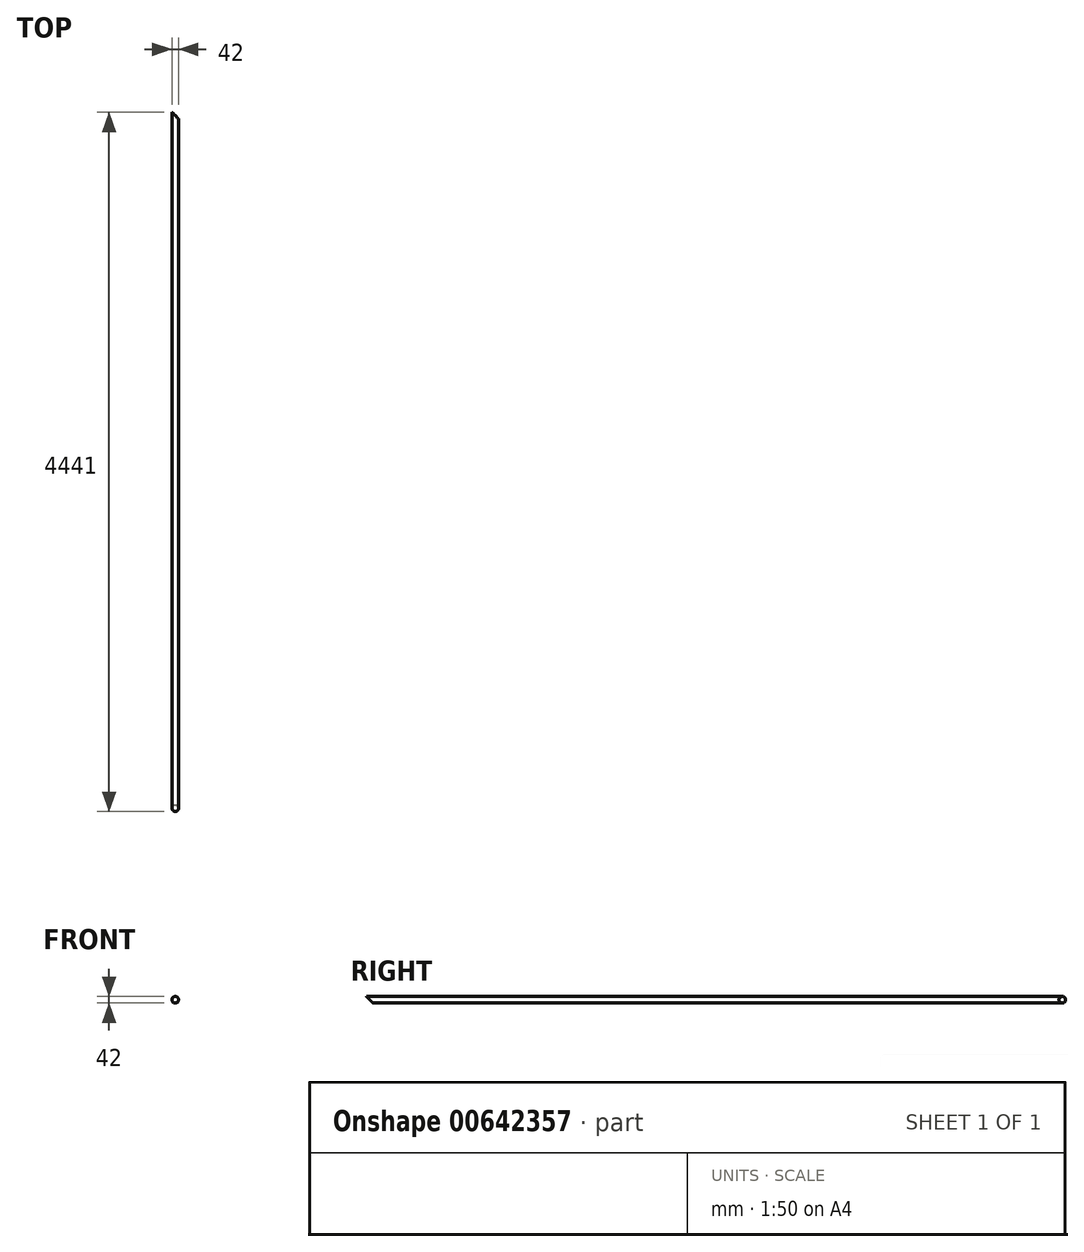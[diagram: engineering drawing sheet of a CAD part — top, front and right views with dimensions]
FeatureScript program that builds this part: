
annotation { "Feature Type Name" : "Feature", "Feature Type Description" : "" }
export const myFeature = defineFeature(function(context is Context, id is Id, definition is map)
    precondition{}
    {
        {
            var Q0;
            Q0=qCreatedBy(makeId("Front.planeOp"),FACE);
            var sketch = newSketch(context, id + "F0", { "sketchPlane" : qUnion([Q0])});
            skLineSegment(sketch, "E0.bottom", {"start": v(21, 21) * mm, "end": v(-21, 21) * mm});
            skLineSegment(sketch, "E0.top", {"start": v(21, -21) * mm, "end": v(-21, -21) * mm});
            skLineSegment(sketch, "E0.left", {"start": v(21, 21) * mm, "end": v(21, -21) * mm});
            skLineSegment(sketch, "E0.right", {"start": v(-21, 21) * mm, "end": v(-21, -21) * mm});
            skPoint(sketch, "E0.middle", {"position": v(0, 0) * mm});
            skSolve(sketch);
        }
        {
            var Q0;
            Q0=makeQuery(id+"F0.imprint","IMPRINT",FACE,{"disambiguationData":[TD([[makeQuery(id+"F0.imprint","IMPRINT",EDGE,{"derivedFrom":sQuery(id+"F0.wireOp",EDGE,"E0.bottom")}),1.0]])]});
            extrude(context, id + "F1", {"entities" : qUnion([Q0]), "depth" : 4441 * mm, "offsetDistance" : 25 * mm});
        }
        {
            var Q0;
            Q0=makeQuery(id+"F1.opExtrude","SWEPT_FACE",FACE,{"disambiguationData":[OSD([sQuery(id+"F0.wireOp",EDGE,"E0.left")])]});
            var sketch = newSketch(context, id + "F2", { "sketchPlane" : qUnion([Q0])});
            skLineSegment(sketch, "E1", {"start": v(-4441, 21) * mm, "end": v(-4399, -21) * mm});
            skSolve(sketch);
        }
        {
            var Q0;
            {var subQ0=sQuery(id+"F2.wireOp",EDGE,"E1");Q0=makeQuery(id+"F2.imprint","IMPRINT",FACE,{"disambiguationData":[TD([[makeQuery(id+"F2.imprint","IMPRINT",EDGE,{"derivedFrom":subQ0}),-1.0]])]});}
            extrude(context, id + "F3", {"entities" : qUnion([Q0]), "operationType" : NewBodyOperationType.REMOVE, "oppositeDirection" : true, "depth" : 100 * mm, "offsetDistance" : 25 * mm});
        }
        {
            var Q0;
            Q0=makeQuery(id+"F1.opExtrude","SWEPT_FACE",FACE,{"disambiguationData":[OSD([sQuery(id+"F0.wireOp",EDGE,"E0.top")])]});
            var sketch = newSketch(context, id + "F4", { "sketchPlane" : qUnion([Q0])});
            skLineSegment(sketch, "E2", {"start": v(-21, 0) * mm, "end": v(21, 42) * mm});
            skSolve(sketch);
        }
        {
            var Q0;
            {var subQ0=sQuery(id+"F4.wireOp",EDGE,"E2");Q0=makeQuery(id+"F4.imprint","IMPRINT",FACE,{"disambiguationData":[TD([[makeQuery(id+"F4.imprint","IMPRINT",EDGE,{"derivedFrom":subQ0}),-1.0]])]});}
            extrude(context, id + "F5", {"entities" : qUnion([Q0]), "operationType" : NewBodyOperationType.REMOVE, "oppositeDirection" : true, "depth" : 100 * mm, "offsetDistance" : 25 * mm});
        }
        {
            var Q0;
            Q0=makeQuery(id+"F1.opExtrude","SWEPT_EDGE",EDGE,{"disambiguationData":[OSD([sQuery(id+"F0.wireOp",EDGE,"E0.top"),sQuery(id+"F0.wireOp",EDGE,"E0.right")])]});
            var Q1;
            Q1=makeQuery(id+"F1.opExtrude","SWEPT_EDGE",EDGE,{"disambiguationData":[OSD([sQuery(id+"F0.wireOp",EDGE,"E0.top"),sQuery(id+"F0.wireOp",EDGE,"E0.left")])]});
            var Q2;
            Q2=makeQuery(id+"F1.opExtrude","SWEPT_EDGE",EDGE,{"disambiguationData":[OSD([sQuery(id+"F0.wireOp",EDGE,"E0.bottom"),sQuery(id+"F0.wireOp",EDGE,"E0.right")])]});
            var Q3;
            Q3=makeQuery(id+"F1.opExtrude","SWEPT_EDGE",EDGE,{"disambiguationData":[OSD([sQuery(id+"F0.wireOp",EDGE,"E0.bottom"),sQuery(id+"F0.wireOp",EDGE,"E0.left")])]});
            fillet(context, id + "F6", {"entities" : qUnion([Q0, Q1, Q2, Q3]), "radius" : 21 * mm, "tangentPropagation" : true, "allowEdgeOverflow" : false});
        }
    });
